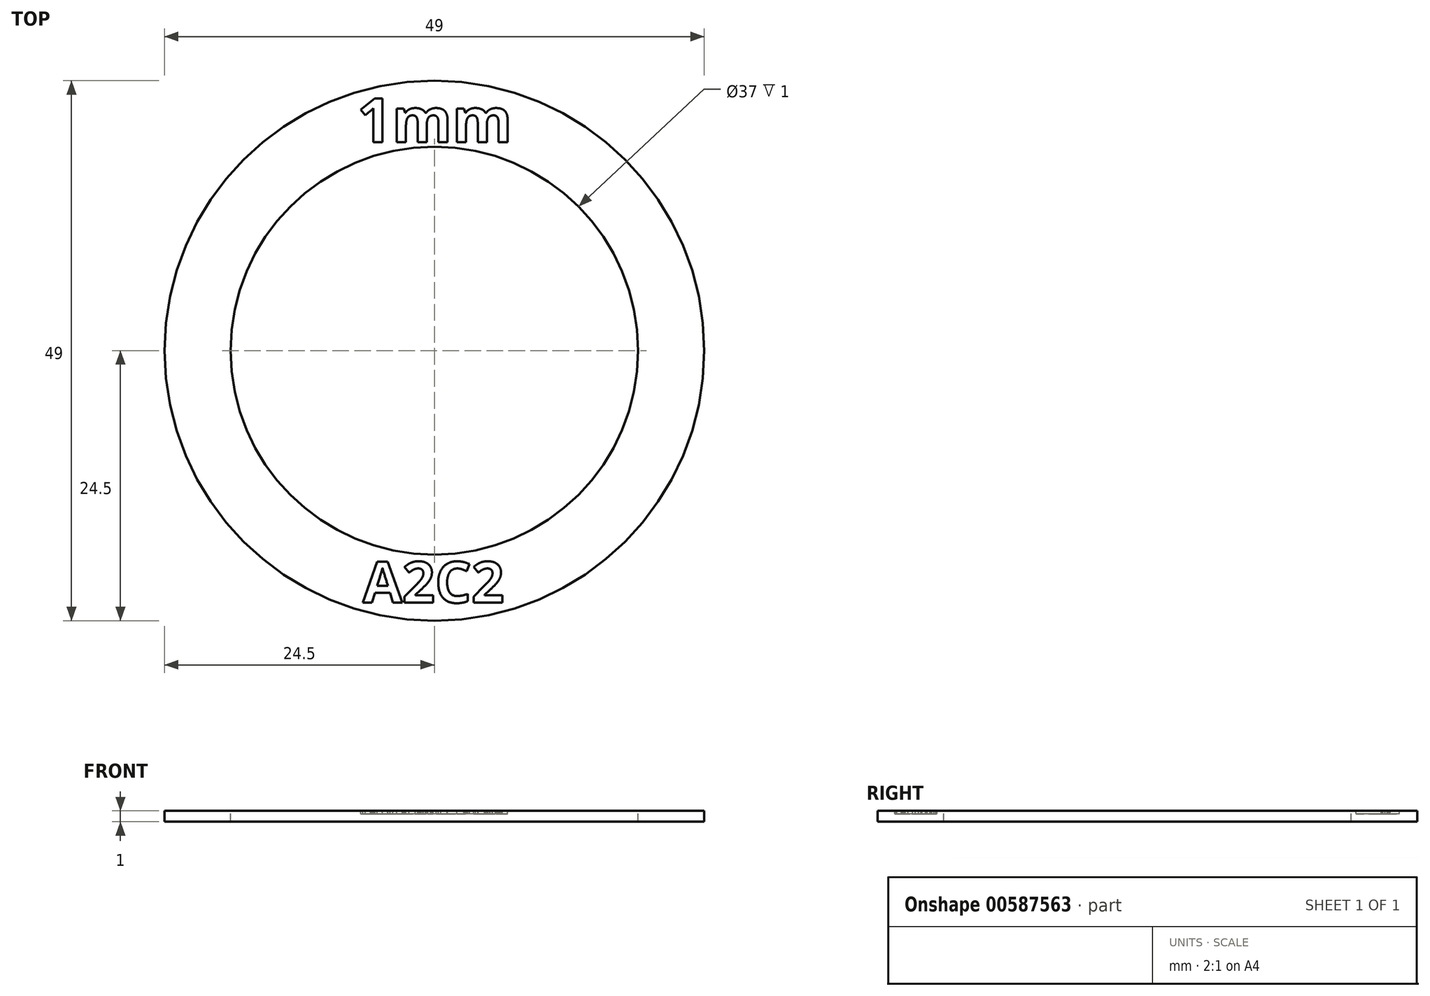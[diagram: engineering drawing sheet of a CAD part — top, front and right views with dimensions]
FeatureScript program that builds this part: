
annotation { "Feature Type Name" : "Feature", "Feature Type Description" : "" }
export const myFeature = defineFeature(function(context is Context, id is Id, definition is map)
    precondition{}
    {
        {
            var Q0;
            Q0=qCreatedBy(makeId("Top.planeOp"),FACE);
            var sketch = newSketch(context, id + "F0", { "sketchPlane" : qUnion([Q0])});
            skCircle(sketch, "E0", {"center": v(0, 0) * mm, "radius": 24.5 * mm});
            skCircle(sketch, "E1", {"center": v(0, 0) * mm, "radius": 18.5 * mm});
            skText(sketch, "E2", { "text": "A2C2", "fontName": "OpenSans-Bold.ttf"});
            skText(sketch, "E3", { "text": "1mm", "fontName": "OpenSans-Bold.ttf"});
            const initialGuessF0  = {"E2": [-0.0065, -0.02287, 1, 0, 0.00374], "E3": [-0.00701, 0.01893, 1, 0, 0.004]};
            skSetInitialGuess(sketch, initialGuessF0);
            skSolve(sketch);
        }
        {
            var Q0;
            Q0=makeQuery(id+"F0.imprint","IMPRINT",FACE,{"disambiguationData":[TD([[makeQuery(id+"F0.imprint","IMPRINT",EDGE,{"derivedFrom":sQuery(id+"F0.wireOp",EDGE,"E2.sketch_text.stroke-8")}),1.0]])]});
            var Q1;
            Q1=makeQuery(id+"F0.imprint","IMPRINT",FACE,{"disambiguationData":[TD([[makeQuery(id+"F0.imprint","IMPRINT",EDGE,{"derivedFrom":sQuery(id+"F0.wireOp",EDGE,"E2.sketch_text.stroke-12")}),-1.0]])]});
            var Q2;
            Q2=makeQuery(id+"F0.imprint","IMPRINT",FACE,{"disambiguationData":[TD([[makeQuery(id+"F0.imprint","IMPRINT",EDGE,{"derivedFrom":sQuery(id+"F0.wireOp",EDGE,"E2.sketch_text.stroke-36")}),-1.0]])]});
            var Q3;
            Q3=makeQuery(id+"F0.imprint","IMPRINT",FACE,{"disambiguationData":[TD([[makeQuery(id+"F0.imprint","IMPRINT",EDGE,{"derivedFrom":sQuery(id+"F0.wireOp",EDGE,"E2.sketch_text.stroke-51")}),-1.0]])]});
            var Q4;
            Q4=makeQuery(id+"F0.imprint","IMPRINT",FACE,{"disambiguationData":[TD([[makeQuery(id+"F0.imprint","IMPRINT",EDGE,{"derivedFrom":sQuery(id+"F0.wireOp",EDGE,"E3.sketch_text.stroke-10")}),-1.0]])]});
            var Q5;
            Q5=makeQuery(id+"F0.imprint","IMPRINT",FACE,{"disambiguationData":[TD([[makeQuery(id+"F0.imprint","IMPRINT",EDGE,{"derivedFrom":sQuery(id+"F0.wireOp",EDGE,"E3.sketch_text.stroke-38")}),-1.0]])]});
            var Q6;
            Q6=makeQuery(id+"F0.imprint","IMPRINT",FACE,{"disambiguationData":[TD([[makeQuery(id+"F0.imprint","IMPRINT",EDGE,{"derivedFrom":sQuery(id+"F0.wireOp",EDGE,"E3.sketch_text.stroke-0")}),-1.0]])]});
            var Q7;
            Q7=makeQuery(id+"F0.imprint","IMPRINT",FACE,{"disambiguationData":[TD([[makeQuery(id+"F0.imprint","IMPRINT",EDGE,{"derivedFrom":sQuery(id+"F0.wireOp",EDGE,"E0")}),1.0]])]});
            var Q8;
            Q8=makeQuery(id+"F0.imprint","IMPRINT",FACE,{"disambiguationData":[TD([[makeQuery(id+"F0.imprint","IMPRINT",EDGE,{"derivedFrom":sQuery(id+"F0.wireOp",EDGE,"E2.sketch_text.stroke-0")}),-1.0]])]});
            extrude(context, id + "F1", {"entities" : qUnion([Q0, Q1, Q2, Q3, Q4, Q5, Q6, Q7, Q8]), "oppositeDirection" : true, "depth" : 1 * mm, "offsetDistance" : 25 * mm});
        }
        {
            var Q0;
            Q0=makeQuery(id+"F0.imprint","IMPRINT",FACE,{"disambiguationData":[TD([[makeQuery(id+"F0.imprint","IMPRINT",EDGE,{"derivedFrom":sQuery(id+"F0.wireOp",EDGE,"E2.sketch_text.stroke-0")}),-1.0]])]});
            var Q1;
            Q1=makeQuery(id+"F0.imprint","IMPRINT",FACE,{"disambiguationData":[TD([[makeQuery(id+"F0.imprint","IMPRINT",EDGE,{"derivedFrom":sQuery(id+"F0.wireOp",EDGE,"E2.sketch_text.stroke-12")}),-1.0]])]});
            var Q2;
            Q2=makeQuery(id+"F0.imprint","IMPRINT",FACE,{"disambiguationData":[TD([[makeQuery(id+"F0.imprint","IMPRINT",EDGE,{"derivedFrom":sQuery(id+"F0.wireOp",EDGE,"E2.sketch_text.stroke-36")}),-1.0]])]});
            var Q3;
            Q3=makeQuery(id+"F0.imprint","IMPRINT",FACE,{"disambiguationData":[TD([[makeQuery(id+"F0.imprint","IMPRINT",EDGE,{"derivedFrom":sQuery(id+"F0.wireOp",EDGE,"E2.sketch_text.stroke-51")}),-1.0]])]});
            var Q4;
            Q4=makeQuery(id+"F0.imprint","IMPRINT",FACE,{"disambiguationData":[TD([[makeQuery(id+"F0.imprint","IMPRINT",EDGE,{"derivedFrom":sQuery(id+"F0.wireOp",EDGE,"E3.sketch_text.stroke-38")}),-1.0]])]});
            var Q5;
            Q5=makeQuery(id+"F0.imprint","IMPRINT",FACE,{"disambiguationData":[TD([[makeQuery(id+"F0.imprint","IMPRINT",EDGE,{"derivedFrom":sQuery(id+"F0.wireOp",EDGE,"E3.sketch_text.stroke-10")}),-1.0]])]});
            var Q6;
            Q6=makeQuery(id+"F0.imprint","IMPRINT",FACE,{"disambiguationData":[TD([[makeQuery(id+"F0.imprint","IMPRINT",EDGE,{"derivedFrom":sQuery(id+"F0.wireOp",EDGE,"E3.sketch_text.stroke-0")}),-1.0]])]});
            extrude(context, id + "F2", {"entities" : qUnion([Q0, Q1, Q2, Q3, Q4, Q5, Q6]), "operationType" : NewBodyOperationType.REMOVE, "oppositeDirection" : true, "depth" : 0.3 * mm, "offsetDistance" : 25 * mm});
        }
    });
